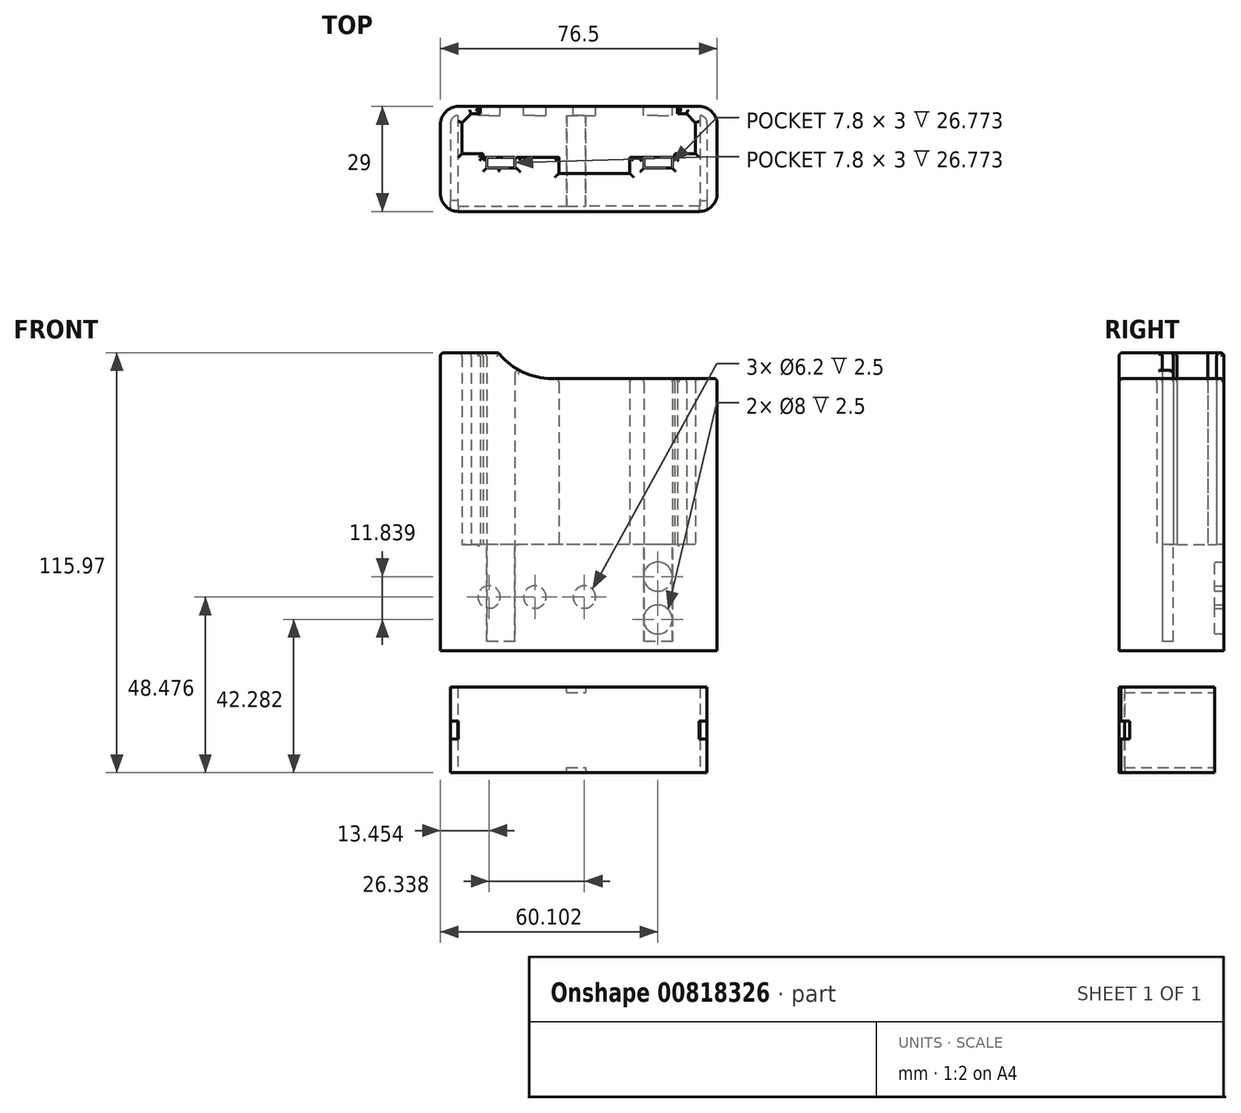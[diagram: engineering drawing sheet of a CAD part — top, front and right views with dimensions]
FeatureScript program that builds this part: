
annotation { "Feature Type Name" : "Feature", "Feature Type Description" : "" }
export const myFeature = defineFeature(function(context is Context, id is Id, definition is map)
    precondition{}
    {
        {
            var Q0;
            Q0=qCreatedBy(makeId("Top.planeOp"),FACE);
            var sketch = newSketch(context, id + "F0", { "sketchPlane" : qUnion([Q0])});
            skLineSegment(sketch, "E0.bottom", {"start": v(32.25, 8) * mm, "end": v(-32.25, 8) * mm});
            skLineSegment(sketch, "E0.top", {"start": v(32.25, -8) * mm, "end": v(-32.25, -8) * mm});
            skLineSegment(sketch, "E0.left", {"start": v(32.25, 8) * mm, "end": v(32.25, -8) * mm});
            skLineSegment(sketch, "E0.right", {"start": v(-32.25, 8) * mm, "end": v(-32.25, -8) * mm});
            skPoint(sketch, "E0.middle", {"position": v(0, 0) * mm});
            skLineSegment(sketch, "E1.bottom", {"start": v(26.5, 9) * mm, "end": v(-26.5, 9) * mm});
            skLineSegment(sketch, "E1.top", {"start": v(26.5, 7) * mm, "end": v(-26.5, 7) * mm});
            skLineSegment(sketch, "E1.left", {"start": v(26.5, 9) * mm, "end": v(26.5, 7) * mm});
            skLineSegment(sketch, "E1.right", {"start": v(-26.5, 9) * mm, "end": v(-26.5, 7) * mm});
            skPoint(sketch, "E1.middle", {"position": v(0, 8) * mm});
            skLineSegment(sketch, "E2.bottom", {"start": v(32.25, -8) * mm, "end": v(38.25, -8) * mm});
            skLineSegment(sketch, "E2.top", {"start": v(32.25, 21) * mm, "end": v(38.25, 21) * mm});
            skLineSegment(sketch, "E2.left", {"start": v(32.25, -8) * mm, "end": v(32.25, 21) * mm});
            skLineSegment(sketch, "E2.right", {"start": v(38.25, -8) * mm, "end": v(38.25, 21) * mm});
            skLineSegment(sketch, "E3.bottom", {"start": v(-32.25, -8) * mm, "end": v(-38.25, -8) * mm});
            skLineSegment(sketch, "E3.top", {"start": v(-32.25, 21) * mm, "end": v(-38.25, 21) * mm});
            skLineSegment(sketch, "E3.left", {"start": v(-32.25, -8) * mm, "end": v(-32.25, 21) * mm});
            skLineSegment(sketch, "E3.right", {"start": v(-38.25, -8) * mm, "end": v(-38.25, 21) * mm});
            skLineSegment(sketch, "E4.bottom", {"start": v(32.25, 21) * mm, "end": v(27.25, 21) * mm});
            skLineSegment(sketch, "E4.top", {"start": v(32.25, 19) * mm, "end": v(27.25, 19) * mm});
            skLineSegment(sketch, "E4.left", {"start": v(32.25, 21) * mm, "end": v(32.25, 19) * mm});
            skLineSegment(sketch, "E4.right", {"start": v(27.25, 21) * mm, "end": v(27.25, 19) * mm});
            skLineSegment(sketch, "E5.bottom", {"start": v(-32.25, 21) * mm, "end": v(-27.25, 21) * mm});
            skLineSegment(sketch, "E5.top", {"start": v(-32.25, 19) * mm, "end": v(-27.25, 19) * mm});
            skLineSegment(sketch, "E5.left", {"start": v(-32.25, 21) * mm, "end": v(-32.25, 19) * mm});
            skLineSegment(sketch, "E5.right", {"start": v(-27.25, 21) * mm, "end": v(-27.25, 19) * mm});
            skLineSegment(sketch, "E6.bottom", {"start": v(-32.25, 19) * mm, "end": v(-29.75, 19) * mm, "construction": true});
            skLineSegment(sketch, "E6.top", {"start": v(-32.25, 16.5) * mm, "end": v(-29.75, 16.5) * mm, "construction": true});
            skLineSegment(sketch, "E6.left", {"start": v(-32.25, 19) * mm, "end": v(-32.25, 16.5) * mm, "construction": true});
            skLineSegment(sketch, "E6.right", {"start": v(-29.75, 19) * mm, "end": v(-29.75, 16.5) * mm, "construction": true});
            skLineSegment(sketch, "E7.bottom", {"start": v(32.25, 19) * mm, "end": v(29.75, 19) * mm, "construction": true});
            skLineSegment(sketch, "E7.top", {"start": v(32.25, 16.5) * mm, "end": v(29.75, 16.5) * mm, "construction": true});
            skLineSegment(sketch, "E7.left", {"start": v(32.25, 19) * mm, "end": v(32.25, 16.5) * mm, "construction": true});
            skLineSegment(sketch, "E7.right", {"start": v(29.75, 19) * mm, "end": v(29.75, 16.5) * mm, "construction": true});
            skLineSegment(sketch, "E8", {"start": v(-32.25, 16.5) * mm, "end": v(-29.75, 19) * mm});
            skLineSegment(sketch, "E9", {"start": v(32.25, 16.5) * mm, "end": v(29.75, 19) * mm});
            skLineSegment(sketch, "E10.bottom", {"start": v(-17.7, 10) * mm, "end": v(-25.5, 10) * mm});
            skLineSegment(sketch, "E10.top", {"start": v(-17.7, 4) * mm, "end": v(-25.5, 4) * mm});
            skLineSegment(sketch, "E10.left", {"start": v(-17.7, 10) * mm, "end": v(-17.7, 4) * mm});
            skLineSegment(sketch, "E10.right", {"start": v(-25.5, 10) * mm, "end": v(-25.5, 4) * mm});
            skPoint(sketch, "E10.middle", {"position": v(-21.6, 7) * mm});
            skLineSegment(sketch, "E11.bottom", {"start": v(25.8, 10) * mm, "end": v(18, 10) * mm});
            skLineSegment(sketch, "E11.top", {"start": v(25.8, 4) * mm, "end": v(18, 4) * mm});
            skLineSegment(sketch, "E11.left", {"start": v(25.8, 10) * mm, "end": v(25.8, 4) * mm});
            skLineSegment(sketch, "E11.right", {"start": v(18, 10) * mm, "end": v(18, 4) * mm});
            skPoint(sketch, "E11.middle", {"position": v(21.9, 7) * mm});
            skLineSegment(sketch, "E12.bottom", {"start": v(14.11, 11.5) * mm, "end": v(8.11, 11.5) * mm});
            skLineSegment(sketch, "E12.top", {"start": v(14.11, 2.5) * mm, "end": v(8.11, 2.5) * mm});
            skLineSegment(sketch, "E12.left", {"start": v(14.11, 11.5) * mm, "end": v(14.11, 2.5) * mm});
            skLineSegment(sketch, "E12.right", {"start": v(8.11, 11.5) * mm, "end": v(8.11, 2.5) * mm});
            skPoint(sketch, "E12.middle", {"position": v(11.11, 7) * mm});
            skLineSegment(sketch, "E13.bottom", {"start": v(0.46, 11.5) * mm, "end": v(-5.54, 11.5) * mm});
            skLineSegment(sketch, "E13.top", {"start": v(0.46, 2.5) * mm, "end": v(-5.54, 2.5) * mm});
            skLineSegment(sketch, "E13.left", {"start": v(0.46, 11.5) * mm, "end": v(0.46, 2.5) * mm});
            skLineSegment(sketch, "E13.right", {"start": v(-5.54, 11.5) * mm, "end": v(-5.54, 2.5) * mm});
            skPoint(sketch, "E13.middle", {"position": v(-2.54, 7) * mm});
            skLineSegment(sketch, "E14.bottom", {"start": v(9.72, 10) * mm, "end": v(1.72, 10) * mm});
            skLineSegment(sketch, "E14.top", {"start": v(9.72, 4) * mm, "end": v(1.72, 4) * mm});
            skLineSegment(sketch, "E14.left", {"start": v(9.72, 10) * mm, "end": v(9.72, 4) * mm});
            skLineSegment(sketch, "E14.right", {"start": v(1.72, 10) * mm, "end": v(1.72, 4) * mm});
            skPoint(sketch, "E14.middle", {"position": v(5.72, 7) * mm});
            skLineSegment(sketch, "E15.bottom", {"start": v(14.11, 11.5) * mm, "end": v(-5.54, 11.5) * mm});
            skLineSegment(sketch, "E15.top", {"start": v(14.11, 2.5) * mm, "end": v(-5.54, 2.5) * mm});
            skSolve(sketch);
        }
        {
            var Q0;
            {var subQ4=sQuery(id+"F0.wireOp",EDGE,"E3.bottom");Q0=makeQuery(id+"F0.imprint","IMPRINT",FACE,{"disambiguationData":[TD([[makeQuery(id+"F0.imprint","IMPRINT",EDGE,{"derivedFrom":subQ4}),-1.0]])]});}
            var Q1;
            Q1=makeQuery(id+"F0.imprint","IMPRINT",FACE,{"disambiguationData":[TD([[makeQuery(id+"F0.imprint","IMPRINT",EDGE,{"derivedFrom":sQuery(id+"F0.wireOp",EDGE,"E5.bottom")}),-1.0]])]});
            var Q2;
            {var subQ3=sQuery(id+"F0.wireOp",EDGE,"E8");Q2=makeQuery(id+"F0.imprint","IMPRINT",FACE,{"disambiguationData":[TD([[makeQuery(id+"F0.imprint","IMPRINT",EDGE,{"derivedFrom":subQ3}),1.0]])]});}
            var Q3;
            {var subQ3=sQuery(id+"F0.wireOp",EDGE,"E9");Q3=makeQuery(id+"F0.imprint","IMPRINT",FACE,{"disambiguationData":[TD([[makeQuery(id+"F0.imprint","IMPRINT",EDGE,{"derivedFrom":subQ3}),-1.0]])]});}
            var Q4;
            {var subQ3=sQuery(id+"F0.wireOp",EDGE,"E2.bottom");Q4=makeQuery(id+"F0.imprint","IMPRINT",FACE,{"disambiguationData":[TD([[makeQuery(id+"F0.imprint","IMPRINT",EDGE,{"derivedFrom":subQ3}),1.0]])]});}
            var Q5;
            Q5=makeQuery(id+"F0.imprint","IMPRINT",FACE,{"disambiguationData":[TD([[makeQuery(id+"F0.imprint","IMPRINT",EDGE,{"derivedFrom":sQuery(id+"F0.wireOp",EDGE,"E4.bottom")}),1.0]])]});
            var Q6;
            {var subQ8=sQuery(id+"F0.wireOp",EDGE,"E0.top");Q6=makeQuery(id+"F0.imprint","IMPRINT",FACE,{"disambiguationData":[TD([[makeQuery(id+"F0.imprint","IMPRINT",EDGE,{"derivedFrom":subQ8}),-1.0]])]});}
            extrude(context, id + "F1", {"entities" : qUnion([Q0, Q1, Q2, Q3, Q4, Q5, Q6]), "depth" : 53 * mm, "offsetDistance" : 25 * mm});
        }
        {
            var Q0;
            Q0=makeQuery(id+"F1.opExtrude","CAP_FACE",FACE,{"disambiguationData":[OSD([sQuery(id+"F0.wireOp",EDGE,"E0.bottom"),sQuery(id+"F0.wireOp",EDGE,"E0.top"),sQuery(id+"F0.wireOp",EDGE,"E1.top"),sQuery(id+"F0.wireOp",EDGE,"E1.left"),sQuery(id+"F0.wireOp",EDGE,"E1.right"),sQuery(id+"F0.wireOp",EDGE,"E2.bottom"),sQuery(id+"F0.wireOp",EDGE,"E2.top"),sQuery(id+"F0.wireOp",EDGE,"E2.left"),sQuery(id+"F0.wireOp",EDGE,"E2.right"),sQuery(id+"F0.wireOp",EDGE,"E3.bottom"),sQuery(id+"F0.wireOp",EDGE,"E3.top"),sQuery(id+"F0.wireOp",EDGE,"E3.left"),sQuery(id+"F0.wireOp",EDGE,"E3.right"),sQuery(id+"F0.wireOp",EDGE,"E4.bottom"),sQuery(id+"F0.wireOp",EDGE,"E4.top"),sQuery(id+"F0.wireOp",EDGE,"E4.right"),sQuery(id+"F0.wireOp",EDGE,"E5.bottom"),sQuery(id+"F0.wireOp",EDGE,"E5.top"),sQuery(id+"F0.wireOp",EDGE,"E5.right"),sQuery(id+"F0.wireOp",EDGE,"E8"),sQuery(id+"F0.wireOp",EDGE,"E9"),sQuery(id+"F0.wireOp",EDGE,"E10.top"),sQuery(id+"F0.wireOp",EDGE,"E10.left"),sQuery(id+"F0.wireOp",EDGE,"E10.right"),sQuery(id+"F0.wireOp",EDGE,"E11.top"),sQuery(id+"F0.wireOp",EDGE,"E11.left"),sQuery(id+"F0.wireOp",EDGE,"E11.right"),sQuery(id+"F0.wireOp",EDGE,"E15.top"),sQuery(id+"F0.wireOp",EDGE,"E12.left"),sQuery(id+"F0.wireOp",EDGE,"E13.right")])],"isStart":true});
            var sketch = newSketch(context, id + "F2", { "sketchPlane" : qUnion([Q0])});
            skLineSegment(sketch, "E16.bottom", {"start": v(38.25, 8) * mm, "end": v(-38.25, 8) * mm});
            skLineSegment(sketch, "E16.top", {"start": v(38.25, -21) * mm, "end": v(-38.25, -21) * mm});
            skLineSegment(sketch, "E16.left", {"start": v(38.25, 8) * mm, "end": v(38.25, -21) * mm});
            skLineSegment(sketch, "E16.right", {"start": v(-38.25, 8) * mm, "end": v(-38.25, -21) * mm});
            skSolve(sketch);
        }
        {
            var Q0;
            Q0=qSketchRegion(id+"F2",true);
            extrude(context, id + "F3", {"entities" : qUnion([Q0]), "operationType" : NewBodyOperationType.ADD, "depth" : 30 * mm, "offsetDistance" : 25 * mm});
        }
        {
            var Q0;
            Q0=makeQuery(id+"F3.boolean.opBoolean","MERGE",FACE,{"derivedFrom":[makeQuery(id+"F1.opExtrude","SWEPT_FACE",FACE,{"disambiguationData":[OSD([sQuery(id+"F0.wireOp",EDGE,"E0.top"),sQuery(id+"F0.wireOp",EDGE,"E2.bottom"),sQuery(id+"F0.wireOp",EDGE,"E3.bottom")])]}),makeQuery(id+"F3.opExtrude","SWEPT_FACE",FACE,{"disambiguationData":[OSD([sQuery(id+"F2.wireOp",EDGE,"E16.bottom")])]})]});
            var sketch = newSketch(context, id + "F4", { "sketchPlane" : qUnion([Q0])});
            skCircle(sketch, "E17", {"center": v(-7.5, 64.6) * mm, "radius": 18.75 * mm});
            skLineSegment(sketch, "E18.bottom", {"start": v(-7.5, 64.6) * mm, "end": v(38.25, 64.6) * mm});
            skLineSegment(sketch, "E18.top", {"start": v(-7.5, 45.85) * mm, "end": v(38.25, 45.85) * mm});
            skLineSegment(sketch, "E18.left", {"start": v(-7.5, 64.6) * mm, "end": v(-7.5, 45.85) * mm});
            skLineSegment(sketch, "E18.right", {"start": v(38.25, 64.6) * mm, "end": v(38.25, 45.85) * mm});
            skLineSegment(sketch, "E19.bottom", {"start": v(38.25, 45.85) * mm, "end": v(11.25, 45.85) * mm});
            skLineSegment(sketch, "E19.top", {"start": v(38.25, 64.6) * mm, "end": v(11.25, 64.6) * mm});
            skLineSegment(sketch, "E19.left", {"start": v(38.25, 45.85) * mm, "end": v(38.25, 64.6) * mm});
            skLineSegment(sketch, "E19.right", {"start": v(11.25, 45.85) * mm, "end": v(11.25, 64.6) * mm});
            skSolve(sketch);
        }
        {
            var Q0;
            {var subQ0=sQuery(id+"F4.wireOp",EDGE,"E18.left");var subQ1=sQuery(id+"F4.wireOp",EDGE,"E17");var subQ2=makeQuery(id+"F4.imprint","INTERSECT",VERTEX,{"derivedFrom":[subQ1,sQuery(id+"F4.wireOp",EDGE,"E18.top"),subQ0]});Q0=makeQuery(id+"F4.imprint","IMPRINT",FACE,{"disambiguationData":[TD([[makeQuery(id+"F4.imprint","IMPRINT",EDGE,{"disambiguationData":[TD([[subQ2,1.0]])],"derivedFrom":subQ1}),1.0]])]});}
            var Q1;
            {var subQ0=sQuery(id+"F4.wireOp",EDGE,"E18.left");var subQ1=sQuery(id+"F4.wireOp",EDGE,"E17");var subQ2=makeQuery(id+"F4.imprint","INTERSECT",VERTEX,{"derivedFrom":[subQ1,sQuery(id+"F4.wireOp",EDGE,"E18.top"),subQ0]});Q1=makeQuery(id+"F4.imprint","IMPRINT",FACE,{"disambiguationData":[TD([[makeQuery(id+"F4.imprint","IMPRINT",EDGE,{"disambiguationData":[TD([[subQ2,-1.0]])],"derivedFrom":subQ1}),1.0]])]});}
            var Q2;
            {var subQ0=sQuery(id+"F4.wireOp",EDGE,"E18.top");Q2=makeQuery(id+"F4.imprint","IMPRINT",FACE,{"disambiguationData":[TD([[makeQuery(id+"F4.imprint","IMPRINT",EDGE,{"derivedFrom":subQ0}),1.0]])]});}
            extrude(context, id + "F5", {"entities" : qUnion([Q0, Q1, Q2]), "operationType" : NewBodyOperationType.REMOVE, "oppositeDirection" : true, "depth" : 32 * mm, "offsetDistance" : 25 * mm});
        }
        {
            var Q0;
            Q0=makeQuery(id+"F3.boolean.opBoolean","MERGE",FACE,{"derivedFrom":[makeQuery(id+"F1.opExtrude","SWEPT_FACE",FACE,{"disambiguationData":[OSD([sQuery(id+"F0.wireOp",EDGE,"E2.top"),sQuery(id+"F0.wireOp",EDGE,"E4.bottom")])]}),makeQuery(id+"F1.opExtrude","SWEPT_FACE",FACE,{"disambiguationData":[OSD([sQuery(id+"F0.wireOp",EDGE,"E3.top"),sQuery(id+"F0.wireOp",EDGE,"E5.bottom")])]}),makeQuery(id+"F3.opExtrude","SWEPT_FACE",FACE,{"disambiguationData":[OSD([sQuery(id+"F2.wireOp",EDGE,"E16.top")])]})]});
            var sketch = newSketch(context, id + "F6", { "sketchPlane" : qUnion([Q0])});
            skCircle(sketch, "E20", {"center": v(-21.85, -8.85) * mm, "radius": 4 * mm});
            skCircle(sketch, "E21", {"center": v(-21.85, -8.85) * mm, "radius": 4.75 * mm, "construction": true});
            skCircle(sketch, "E22", {"center": v(-21.85, -20.69) * mm, "radius": 4 * mm});
            skCircle(sketch, "E23", {"center": v(-21.85, -20.69) * mm, "radius": 4.75 * mm, "construction": true});
            skCircle(sketch, "E24", {"center": v(-1.54, -14.5) * mm, "radius": 3.1 * mm});
            skCircle(sketch, "E25", {"center": v(12.13, -14.5) * mm, "radius": 3.1 * mm});
            skCircle(sketch, "E26", {"center": v(24.8, -14.5) * mm, "radius": 3.1 * mm});
            skSolve(sketch);
        }
        {
            var Q0;
            Q0=makeQuery(id+"F6.imprint","IMPRINT",FACE,{"disambiguationData":[TD([[makeQuery(id+"F6.imprint","IMPRINT",EDGE,{"derivedFrom":sQuery(id+"F6.wireOp",EDGE,"E20")}),1.0]])]});
            var Q1;
            Q1=makeQuery(id+"F6.imprint","IMPRINT",FACE,{"disambiguationData":[TD([[makeQuery(id+"F6.imprint","IMPRINT",EDGE,{"derivedFrom":sQuery(id+"F6.wireOp",EDGE,"E22")}),1.0]])]});
            var Q2;
            Q2=makeQuery(id+"F6.imprint","IMPRINT",FACE,{"disambiguationData":[TD([[makeQuery(id+"F6.imprint","IMPRINT",EDGE,{"derivedFrom":sQuery(id+"F6.wireOp",EDGE,"E24")}),1.0]])]});
            var Q3;
            Q3=makeQuery(id+"F6.imprint","IMPRINT",FACE,{"disambiguationData":[TD([[makeQuery(id+"F6.imprint","IMPRINT",EDGE,{"derivedFrom":sQuery(id+"F6.wireOp",EDGE,"E25")}),1.0]])]});
            var Q4;
            Q4=makeQuery(id+"F6.imprint","IMPRINT",FACE,{"disambiguationData":[TD([[makeQuery(id+"F6.imprint","IMPRINT",EDGE,{"derivedFrom":sQuery(id+"F6.wireOp",EDGE,"E26")}),1.0]])]});
            extrude(context, id + "F7", {"entities" : qUnion([Q0, Q1, Q2, Q3, Q4]), "operationType" : NewBodyOperationType.REMOVE, "oppositeDirection" : true, "depth" : 30 * mm, "offsetDistance" : 25 * mm});
        }
        {
            var Q0;
            Q0=makeQuery(id+"F3.boolean.opBoolean","MERGE",FACE,{"derivedFrom":[makeQuery(id+"F1.opExtrude","SWEPT_FACE",FACE,{"disambiguationData":[OSD([sQuery(id+"F0.wireOp",EDGE,"E0.top"),sQuery(id+"F0.wireOp",EDGE,"E2.bottom"),sQuery(id+"F0.wireOp",EDGE,"E3.bottom")])]}),makeQuery(id+"F3.opExtrude","SWEPT_FACE",FACE,{"disambiguationData":[OSD([sQuery(id+"F2.wireOp",EDGE,"E16.bottom")])]})]});
            var sketch = newSketch(context, id + "F8", { "sketchPlane" : qUnion([Q0])});
            skLineSegment(sketch, "E27.bottom", {"start": v(-35.41, -26.77) * mm, "end": v(35.45, -26.77) * mm});
            skLineSegment(sketch, "E27.top", {"start": v(-35.41, -2.97) * mm, "end": v(35.45, -2.97) * mm});
            skLineSegment(sketch, "E27.left", {"start": v(-35.41, -26.77) * mm, "end": v(-35.41, -2.97) * mm});
            skLineSegment(sketch, "E27.right", {"start": v(35.45, -26.77) * mm, "end": v(35.45, -2.97) * mm});
            skSolve(sketch);
        }
        {
            var Q0;
            Q0=makeQuery(id+"F8.imprint","IMPRINT",FACE,{"disambiguationData":[TD([[makeQuery(id+"F8.imprint","IMPRINT",EDGE,{"derivedFrom":sQuery(id+"F8.wireOp",EDGE,"E27.bottom")}),1.0]])]});
            extrude(context, id + "F9", {"entities" : qUnion([Q0]), "operationType" : NewBodyOperationType.REMOVE, "oppositeDirection" : true, "depth" : 26.5 * mm, "offsetDistance" : 25 * mm});
        }
        {
            var Q0;
            Q0=makeQuery(id+"F3.opExtrude","CAP_FACE",FACE,{"disambiguationData":[OSD([sQuery(id+"F2.wireOp",EDGE,"E16.bottom"),sQuery(id+"F2.wireOp",EDGE,"E16.top"),sQuery(id+"F2.wireOp",EDGE,"E16.left"),sQuery(id+"F2.wireOp",EDGE,"E16.right")])],"isStart":true});
            var sketch = newSketch(context, id + "F10", { "sketchPlane" : qUnion([Q0])});
            skLineSegment(sketch, "E28.bottom", {"start": v(25.8, 4) * mm, "end": v(18, 4) * mm});
            skLineSegment(sketch, "E28.top", {"start": v(25.8, 7) * mm, "end": v(18, 7) * mm});
            skLineSegment(sketch, "E28.left", {"start": v(25.8, 4) * mm, "end": v(25.8, 7) * mm});
            skLineSegment(sketch, "E28.right", {"start": v(18, 4) * mm, "end": v(18, 7) * mm});
            skLineSegment(sketch, "E29.bottom", {"start": v(-17.7, 4) * mm, "end": v(-25.5, 4) * mm});
            skLineSegment(sketch, "E29.top", {"start": v(-17.7, 7) * mm, "end": v(-25.5, 7) * mm});
            skLineSegment(sketch, "E29.left", {"start": v(-17.7, 4) * mm, "end": v(-17.7, 7) * mm});
            skLineSegment(sketch, "E29.right", {"start": v(-25.5, 4) * mm, "end": v(-25.5, 7) * mm});
            skSolve(sketch);
        }
        {
            var Q0;
            Q0=makeQuery(id+"F10.imprint","IMPRINT",FACE,{"disambiguationData":[TD([[makeQuery(id+"F10.imprint","IMPRINT",EDGE,{"derivedFrom":sQuery(id+"F10.wireOp",EDGE,"E28.bottom")}),-1.0]])]});
            var Q1;
            Q1=makeQuery(id+"F10.imprint","IMPRINT",FACE,{"disambiguationData":[TD([[makeQuery(id+"F10.imprint","IMPRINT",EDGE,{"derivedFrom":sQuery(id+"F10.wireOp",EDGE,"E29.bottom")}),-1.0]])]});
            extrude(context, id + "F11", {"entities" : qUnion([Q0, Q1]), "operationType" : NewBodyOperationType.REMOVE, "oppositeDirection" : true, "depth" : 6 * mm, "offsetDistance" : 25 * mm});
        }
        {
            var Q0;
            Q0=makeQuery(id+"F3.boolean.opBoolean","MERGE",EDGE,{"derivedFrom":[makeQuery(id+"F1.opExtrude","SWEPT_EDGE",EDGE,{"disambiguationData":[OSD([sQuery(id+"F0.wireOp",EDGE,"E2.bottom"),sQuery(id+"F0.wireOp",EDGE,"E2.right")])]}),makeQuery(id+"F3.opExtrude","SWEPT_EDGE",EDGE,{"disambiguationData":[OSD([sQuery(id+"F2.wireOp",EDGE,"E16.bottom"),sQuery(id+"F2.wireOp",EDGE,"E16.left")])]})]});
            var Q1;
            Q1=makeQuery(id+"F3.boolean.opBoolean","MERGE",EDGE,{"derivedFrom":[makeQuery(id+"F1.opExtrude","SWEPT_EDGE",EDGE,{"disambiguationData":[OSD([sQuery(id+"F0.wireOp",EDGE,"E3.bottom"),sQuery(id+"F0.wireOp",EDGE,"E3.right")])]}),makeQuery(id+"F3.opExtrude","SWEPT_EDGE",EDGE,{"disambiguationData":[OSD([sQuery(id+"F2.wireOp",EDGE,"E16.bottom"),sQuery(id+"F2.wireOp",EDGE,"E16.right")])]})]});
            var Q2;
            Q2=makeQuery(id+"F3.boolean.opBoolean","MERGE",EDGE,{"derivedFrom":[makeQuery(id+"F1.opExtrude","SWEPT_EDGE",EDGE,{"disambiguationData":[OSD([sQuery(id+"F0.wireOp",EDGE,"E3.top"),sQuery(id+"F0.wireOp",EDGE,"E3.right")])]}),makeQuery(id+"F3.opExtrude","SWEPT_EDGE",EDGE,{"disambiguationData":[OSD([sQuery(id+"F2.wireOp",EDGE,"E16.top"),sQuery(id+"F2.wireOp",EDGE,"E16.right")])]})]});
            var Q3;
            Q3=makeQuery(id+"F3.boolean.opBoolean","MERGE",EDGE,{"derivedFrom":[makeQuery(id+"F1.opExtrude","SWEPT_EDGE",EDGE,{"disambiguationData":[OSD([sQuery(id+"F0.wireOp",EDGE,"E2.top"),sQuery(id+"F0.wireOp",EDGE,"E2.right")])]}),makeQuery(id+"F3.opExtrude","SWEPT_EDGE",EDGE,{"disambiguationData":[OSD([sQuery(id+"F2.wireOp",EDGE,"E16.top"),sQuery(id+"F2.wireOp",EDGE,"E16.left")])]})]});
            fillet(context, id + "F12", {"entities" : qUnion([Q0, Q1, Q2, Q3]), "radius" : 5 * mm, "tangentPropagation" : true, "allowEdgeOverflow" : false});
        }
        {
            var Q0;
            Q0=makeQuery(id+"F1.opExtrude","CAP_FACE",FACE,{"disambiguationData":[OSD([sQuery(id+"F0.wireOp",EDGE,"E0.bottom"),sQuery(id+"F0.wireOp",EDGE,"E0.top"),sQuery(id+"F0.wireOp",EDGE,"E1.top"),sQuery(id+"F0.wireOp",EDGE,"E1.left"),sQuery(id+"F0.wireOp",EDGE,"E1.right"),sQuery(id+"F0.wireOp",EDGE,"E2.bottom"),sQuery(id+"F0.wireOp",EDGE,"E2.top"),sQuery(id+"F0.wireOp",EDGE,"E2.left"),sQuery(id+"F0.wireOp",EDGE,"E2.right"),sQuery(id+"F0.wireOp",EDGE,"E3.bottom"),sQuery(id+"F0.wireOp",EDGE,"E3.top"),sQuery(id+"F0.wireOp",EDGE,"E3.left"),sQuery(id+"F0.wireOp",EDGE,"E3.right"),sQuery(id+"F0.wireOp",EDGE,"E4.bottom"),sQuery(id+"F0.wireOp",EDGE,"E4.top"),sQuery(id+"F0.wireOp",EDGE,"E4.right"),sQuery(id+"F0.wireOp",EDGE,"E5.bottom"),sQuery(id+"F0.wireOp",EDGE,"E5.top"),sQuery(id+"F0.wireOp",EDGE,"E5.right"),sQuery(id+"F0.wireOp",EDGE,"E8"),sQuery(id+"F0.wireOp",EDGE,"E9"),sQuery(id+"F0.wireOp",EDGE,"E10.top"),sQuery(id+"F0.wireOp",EDGE,"E10.left"),sQuery(id+"F0.wireOp",EDGE,"E10.right"),sQuery(id+"F0.wireOp",EDGE,"E11.top"),sQuery(id+"F0.wireOp",EDGE,"E11.left"),sQuery(id+"F0.wireOp",EDGE,"E11.right"),sQuery(id+"F0.wireOp",EDGE,"E15.top"),sQuery(id+"F0.wireOp",EDGE,"E12.left"),sQuery(id+"F0.wireOp",EDGE,"E13.right")])],"isStart":false});
            var Q1;
            Q1=makeQuery(id+"F5.boolean.opBoolean","COPY",FACE,{"derivedFrom":makeQuery(id+"F5.opExtrude","SWEPT_FACE",FACE,{"disambiguationData":[OSD([sQuery(id+"F4.wireOp",EDGE,"O5dZKBO2-Gea2-ohxR-MJXU-QaXSxVA7yxUH.top")])]})});
            var Q2;
            Q2=makeQuery(id+"F5.boolean.opBoolean","COPY",FACE,{"derivedFrom":makeQuery(id+"F5.opExtrude","SWEPT_FACE",FACE,{"disambiguationData":[OSD([sQuery(id+"F4.wireOp",EDGE,"E18.top")])]})});
            fillet(context, id + "F13", {"entities" : qUnion([Q0, Q1, Q2]), "radius" : 1 * mm, "tangentPropagation" : true, "allowEdgeOverflow" : false});
        }
        {
            var Q0;
            Q0=makeQuery(id+"F5.boolean.opBoolean","COPY",FACE,{"derivedFrom":makeQuery(id+"F5.opExtrude","SWEPT_FACE",FACE,{"disambiguationData":[OSD([sQuery(id+"F4.wireOp",EDGE,"E17")])]})});
            fillet(context, id + "F14", {"entities" : qUnion([Q0]), "radius" : 1 * mm, "tangentPropagation" : true, "allowEdgeOverflow" : false});
        }
        {
            var Q0;
            Q0=makeQuery(id+"F1.opExtrude","SWEPT_EDGE",EDGE,{"disambiguationData":[OSD([sQuery(id+"F0.wireOp",EDGE,"E4.bottom"),sQuery(id+"F0.wireOp",EDGE,"E4.right")])]});
            var Q1;
            Q1=makeQuery(id+"F3.opExtrude","CAP_EDGE",EDGE,{"disambiguationData":[OSD([sQuery(id+"F2.wireOp",EDGE,"E16.top")])],"isStart":true});
            var Q2;
            Q2=makeQuery(id+"F1.opExtrude","SWEPT_EDGE",EDGE,{"disambiguationData":[OSD([sQuery(id+"F0.wireOp",EDGE,"E5.bottom"),sQuery(id+"F0.wireOp",EDGE,"E5.right")])]});
            fillet(context, id + "F15", {"entities" : qUnion([Q0, Q1, Q2]), "radius" : .5 * mm, "tangentPropagation" : true, "allowEdgeOverflow" : false});
        }
        {
            var Q0;
            Q0=makeQuery(id+"F3.opExtrude","CAP_FACE",FACE,{"disambiguationData":[OSD([sQuery(id+"F2.wireOp",EDGE,"E16.bottom"),sQuery(id+"F2.wireOp",EDGE,"E16.top"),sQuery(id+"F2.wireOp",EDGE,"E16.left"),sQuery(id+"F2.wireOp",EDGE,"E16.right")])],"isStart":false});
            var sketch = newSketch(context, id + "F16", { "sketchPlane" : qUnion([Q0])});
            skCircle(sketch, "E30", {"center": v(11.1, -12.06) * mm, "radius": 3.75 * mm});
            skCircle(sketch, "E31", {"center": v(11.1, 0) * mm, "radius": 3.75 * mm});
            skSolve(sketch);
        }
        {
            var Q0;
            Q0=makeQuery(id+"F16.imprint","IMPRINT",FACE,{"disambiguationData":[TD([[makeQuery(id+"F16.imprint","IMPRINT",EDGE,{"derivedFrom":sQuery(id+"F16.wireOp",EDGE,"E30")}),1.0]])]});
            var Q1;
            Q1=makeQuery(id+"F16.imprint","IMPRINT",FACE,{"disambiguationData":[TD([[makeQuery(id+"F16.imprint","IMPRINT",EDGE,{"derivedFrom":sQuery(id+"F16.wireOp",EDGE,"E31")}),1.0]])]});
            extrude(context, id + "F17", {"entities" : qUnion([Q0, Q1]), "operationType" : NewBodyOperationType.REMOVE, "oppositeDirection" : true, "depth" : 5 * mm, "offsetDistance" : 25 * mm});
        }
        {
            var Q0;
            Q0=makeQuery(id+"F9.boolean.opBoolean","COPY",EDGE,{"derivedFrom":makeQuery(id+"F9.opExtrude","CAP_EDGE",EDGE,{"disambiguationData":[OSD([sQuery(id+"F8.wireOp",EDGE,"E27.left")])],"isStart":false})});
            var Q1;
            Q1=makeQuery(id+"F9.boolean.opBoolean","COPY",EDGE,{"derivedFrom":makeQuery(id+"F9.opExtrude","CAP_EDGE",EDGE,{"disambiguationData":[OSD([sQuery(id+"F8.wireOp",EDGE,"E27.right")])],"isStart":false})});
            fillet(context, id + "F18", {"entities" : qUnion([Q0, Q1]), "radius" : 2 * mm, "tangentPropagation" : true, "allowEdgeOverflow" : false});
        }
        {
            var Q0;
            Q0=makeQuery(id+"F9.boolean.opBoolean","COPY",FACE,{"derivedFrom":makeQuery(id+"F9.opExtrude","SWEPT_FACE",FACE,{"disambiguationData":[OSD([sQuery(id+"F8.wireOp",EDGE,"E27.top")])]})});
            extrude(context, id + "F19", {"entities" : qUnion([Q0]), "operationType" : NewBodyOperationType.ADD, "depth" : 60 * mm, "offsetDistance" : 25 * mm});
        }
        {
            var Q0;
            Q0=makeQuery(id+"F19.opExtrude","CAP_FACE",FACE,{"disambiguationData":[OSD([sQuery(id+"F8.wireOp",EDGE,"E27.top")])],"isStart":false});
            cPlane(context, id + "F20", {"entities" : qUnion([Q0]), "cplaneType" : CPlaneType.OFFSET, "offset" : 23.6 * mm, "oppositeDirection" : true, "width" : 150 * mm, "height" : 150 * mm});
        }
        {
            var Q0;
            Q0=qCreatedBy(id+"F20.planeOp",FACE);
            var sketch = newSketch(context, id + "F21", { "sketchPlane" : qUnion([Q0])});
            skLineSegment(sketch, "E32.bottom", {"start": v(39.94, -22.98) * mm, "end": v(-41.19, -22.98) * mm});
            skLineSegment(sketch, "E32.top", {"start": v(39.94, 13.76) * mm, "end": v(-41.19, 13.76) * mm});
            skLineSegment(sketch, "E32.left", {"start": v(39.94, -22.98) * mm, "end": v(39.94, 13.76) * mm});
            skLineSegment(sketch, "E32.right", {"start": v(-41.19, -22.98) * mm, "end": v(-41.19, 13.76) * mm});
            skSolve(sketch);
        }
        {
            var Q0;
            Q0 = qSketchRegion(id + "F21", true);
            extrude(context, id + "F22", {"entities" : qUnion([Q0]), "operationType" : NewBodyOperationType.REMOVE, "oppositeDirection" : true, "depth" : 10 * mm, "offsetDistance" : 25 * mm});
        }
        {
            var Q0;
            Q0=makeQuery(id+"F19.opExtrude","CAP_FACE",FACE,{"disambiguationData":[OSD([sQuery(id+"F8.wireOp",EDGE,"E27.top")])],"isStart":false});
            var sketch = newSketch(context, id + "F23", { "sketchPlane" : qUnion([Q0])});
            skLineSegment(sketch, "E33.bottom", {"start": v(-33.41, -18.5) * mm, "end": v(-3.3, -18.5) * mm});
            skLineSegment(sketch, "E33.top", {"start": v(-33.41, 6.5) * mm, "end": v(-3.3, 6.5) * mm});
            skLineSegment(sketch, "E33.left", {"start": v(-33.41, -18.5) * mm, "end": v(-33.41, 6.5) * mm});
            skLineSegment(sketch, "E33.right", {"start": v(-3.3, -18.5) * mm, "end": v(-3.3, 6.5) * mm});
            skLineSegment(sketch, "E34.bottom", {"start": v(33.45, -18.5) * mm, "end": v(1.86, -18.5) * mm});
            skLineSegment(sketch, "E34.top", {"start": v(33.45, 6.5) * mm, "end": v(1.86, 6.5) * mm});
            skLineSegment(sketch, "E34.left", {"start": v(33.45, -18.5) * mm, "end": v(33.45, 6.5) * mm});
            skLineSegment(sketch, "E34.right", {"start": v(1.86, -18.5) * mm, "end": v(1.86, 6.5) * mm});
            skSolve(sketch);
        }
        {
            var Q0;
            Q0=makeQuery(id+"F23.imprint","IMPRINT",FACE,{"disambiguationData":[TD([[makeQuery(id+"F23.imprint","IMPRINT",EDGE,{"derivedFrom":sQuery(id+"F23.wireOp",EDGE,"E33.bottom")}),1.0]])]});
            var Q1;
            Q1=makeQuery(id+"F23.imprint","IMPRINT",FACE,{"disambiguationData":[TD([[makeQuery(id+"F23.imprint","IMPRINT",EDGE,{"derivedFrom":sQuery(id+"F23.wireOp",EDGE,"E34.bottom")}),1.0]])]});
            extrude(context, id + "F24", {"entities" : qUnion([Q0, Q1]), "operationType" : NewBodyOperationType.REMOVE, "oppositeDirection" : true, "depth" : 25 * mm, "offsetDistance" : 25 * mm});
        }
        {
            var Q0;
            {var subQ0=sQuery(id+"F8.wireOp",EDGE,"E27.top");Q0=makeQuery(id+"F19.boolean.opBoolean","SPLIT",FACE,{"disambiguationData":[TD([makeQuery(id+"F19.opExtrude","CAP_FACE",FACE,{"disambiguationData":[OSD([subQ0])],"isStart":false})])],"derivedFrom":makeQuery(id+"F19.opExtrude","SWEPT_FACE",FACE,{"disambiguationData":[OSD([subQ0]),TDD([makeQuery(id+"F9.boolean.opBoolean","COPY",EDGE,{"derivedFrom":makeQuery(id+"F9.opExtrude","CAP_EDGE",EDGE,{"disambiguationData":[OSD([subQ0])],"isStart":false})})])]})});}
            var sketch = newSketch(context, id + "F25", { "sketchPlane" : qUnion([Q0])});
            skLineSegment(sketch, "E35.bottom", {"start": v(3.3, -40.95) * mm, "end": v(-1.86, -40.95) * mm});
            skLineSegment(sketch, "E35.top", {"start": v(3.3, -61.54) * mm, "end": v(-1.86, -61.54) * mm});
            skLineSegment(sketch, "E35.left", {"start": v(3.3, -40.95) * mm, "end": v(3.3, -61.54) * mm});
            skLineSegment(sketch, "E35.right", {"start": v(-1.86, -40.95) * mm, "end": v(-1.86, -61.54) * mm});
            skSolve(sketch);
        }
        {
            var Q0;
            Q0=makeQuery(id+"F25.imprint","IMPRINT",FACE,{"disambiguationData":[TD([[makeQuery(id+"F25.imprint","IMPRINT",EDGE,{"derivedFrom":sQuery(id+"F25.wireOp",EDGE,"E35.bottom")}),1.0]])]});
            extrude(context, id + "F26", {"entities" : qUnion([Q0]), "operationType" : NewBodyOperationType.REMOVE, "oppositeDirection" : true, "depth" : 25 * mm, "offsetDistance" : 25 * mm});
        }
        {
            var Q0;
            {var subQ0=sQuery(id+"F8.wireOp",EDGE,"E27.top");var subQ2=sQuery(id+"F2.wireOp",EDGE,"E16.bottom");var subQ4=sQuery(id+"F0.wireOp",EDGE,"E3.bottom");var subQ7=sQuery(id+"F0.wireOp",EDGE,"E2.bottom");var subQ8=makeQuery(id+"F3.boolean.opBoolean","MERGE",FACE,{"derivedFrom":[makeQuery(id+"F1.opExtrude","SWEPT_FACE",FACE,{"disambiguationData":[OSD([sQuery(id+"F0.wireOp",EDGE,"E0.top"),subQ7,subQ4])]}),makeQuery(id+"F3.opExtrude","SWEPT_FACE",FACE,{"disambiguationData":[OSD([subQ2])]})]});Q0=makeQuery(id+"F22.boolean.opBoolean","SPLIT",FACE,{"disambiguationData":[TD([makeQuery(id+"F19.opExtrude","CAP_FACE",FACE,{"disambiguationData":[OSD([subQ0])],"isStart":false})])],"derivedFrom":makeQuery(id+"F19.boolean.opBoolean","MERGE",FACE,{"derivedFrom":[makeQuery(id+"F12.opFillet","SPLIT",FACE,{"disambiguationData":[OD(1.0)],"derivedFrom":subQ8}),makeQuery(id+"F12.opFillet","SPLIT",FACE,{"disambiguationData":[OD(0.0)],"derivedFrom":subQ8}),makeQuery(id+"F19.opExtrude","SWEPT_FACE",FACE,{"disambiguationData":[OSD([subQ0]),TDD([makeQuery(id+"F9.boolean.opBoolean","COPY",EDGE,{"derivedFrom":makeQuery(id+"F9.opExtrude","CAP_EDGE",EDGE,{"disambiguationData":[OSD([subQ0])],"isStart":true})})])]})]})});}
            var sketch = newSketch(context, id + "F27", { "sketchPlane" : qUnion([Q0])});
            skLineSegment(sketch, "E36.bottom", {"start": v(33.25, -48.75) * mm, "end": v(35.75, -48.75) * mm});
            skLineSegment(sketch, "E36.top", {"start": v(33.25, -53.75) * mm, "end": v(35.75, -53.75) * mm});
            skLineSegment(sketch, "E36.left", {"start": v(33.25, -48.75) * mm, "end": v(33.25, -53.75) * mm});
            skLineSegment(sketch, "E36.right", {"start": v(35.75, -48.75) * mm, "end": v(35.75, -53.75) * mm});
            skLineSegment(sketch, "E37.bottom", {"start": v(-33.25, -53.75) * mm, "end": v(-35.75, -53.75) * mm});
            skLineSegment(sketch, "E37.top", {"start": v(-33.25, -48.75) * mm, "end": v(-35.75, -48.75) * mm});
            skLineSegment(sketch, "E37.left", {"start": v(-33.25, -53.75) * mm, "end": v(-33.25, -48.75) * mm});
            skLineSegment(sketch, "E37.right", {"start": v(-35.75, -53.75) * mm, "end": v(-35.75, -48.75) * mm});
            skSolve(sketch);
        }
        {
            var Q0;
            Q0=makeQuery(id+"F27.imprint","IMPRINT",FACE,{"disambiguationData":[TD([[makeQuery(id+"F27.imprint","IMPRINT",EDGE,{"derivedFrom":sQuery(id+"F27.wireOp",EDGE,"E36.bottom")}),-1.0]])]});
            var Q1;
            Q1=makeQuery(id+"F27.imprint","IMPRINT",FACE,{"disambiguationData":[TD([[makeQuery(id+"F27.imprint","IMPRINT",EDGE,{"derivedFrom":sQuery(id+"F27.wireOp",EDGE,"E37.bottom")}),-1.0]])]});
            extrude(context, id + "F28", {"entities" : qUnion([Q0, Q1]), "operationType" : NewBodyOperationType.REMOVE, "oppositeDirection" : true, "depth" : 3 * mm, "offsetDistance" : 25 * mm});
        }
    });
